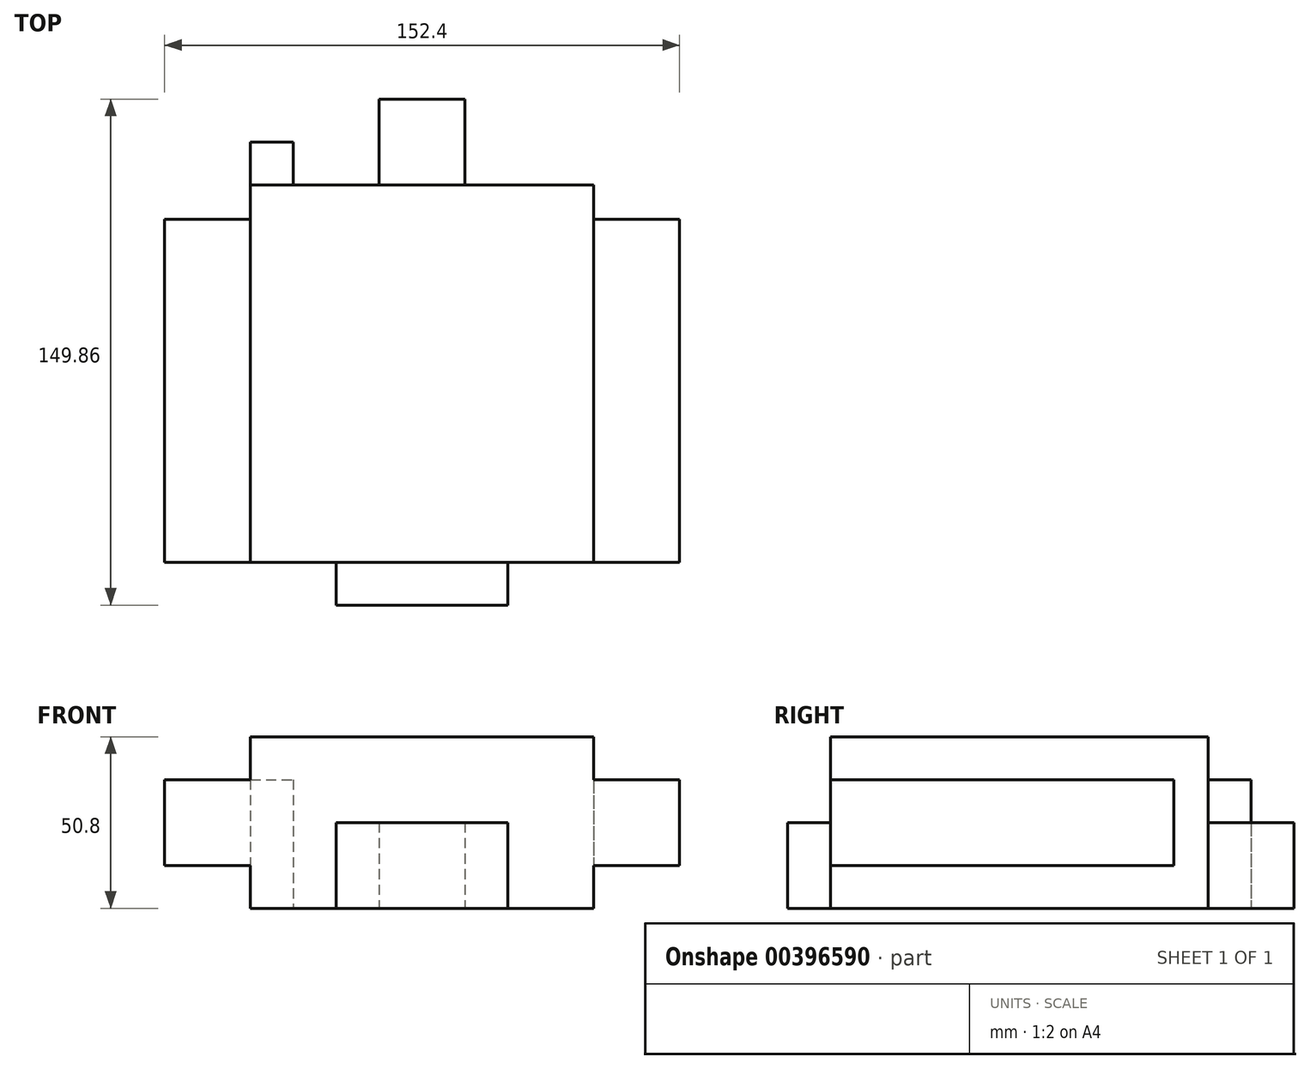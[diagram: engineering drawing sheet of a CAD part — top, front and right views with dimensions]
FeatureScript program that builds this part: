
annotation { "Feature Type Name" : "Feature", "Feature Type Description" : "" }
export const myFeature = defineFeature(function(context is Context, id is Id, definition is map)
    precondition{}
    {
        {
            var Q0;
            Q0=qCreatedBy(makeId("Top.planeOp"),FACE);
            var sketch = newSketch(context, id + "F0", { "sketchPlane" : qUnion([Q0])});
            skLineSegment(sketch, "E0.left", {"start": v(-50.8, -55.88) * mm, "end": v(-50.8, 55.88) * mm});
            skLineSegment(sketch, "E0.right", {"start": v(50.8, -55.88) * mm, "end": v(50.8, 55.88) * mm});
            skLineSegment(sketch, "E1", {"start": v(50.8, -55.88) * mm, "end": v(25.4, -55.88) * mm});
            skLineSegment(sketch, "E2", {"start": v(-25.4, -55.88) * mm, "end": v(-50.8, -55.88) * mm});
            skLineSegment(sketch, "E3.left", {"start": v(-25.4, -55.88) * mm, "end": v(-25.4, -55.88) * mm});
            skLineSegment(sketch, "E3.right", {"start": v(25.4, -55.88) * mm, "end": v(25.4, -55.88) * mm});
            skLineSegment(sketch, "E4.top", {"start": v(-25.4, -68.58) * mm, "end": v(25.4, -68.58) * mm});
            skLineSegment(sketch, "E4.left", {"start": v(-25.4, -55.88) * mm, "end": v(-25.4, -68.58) * mm});
            skLineSegment(sketch, "E4.right", {"start": v(25.4, -55.88) * mm, "end": v(25.4, -68.58) * mm});
            skLineSegment(sketch, "E5", {"start": v(25.4, -68.58) * mm, "end": v(12.7, -68.58) * mm});
            skLineSegment(sketch, "E6", {"start": v(-25.4, -68.58) * mm, "end": v(-12.7, -68.58) * mm});
            skLineSegment(sketch, "E7.left", {"start": v(-12.7, 55.88) * mm, "end": v(-12.7, 55.88) * mm});
            skLineSegment(sketch, "E7.right", {"start": v(12.7, 55.88) * mm, "end": v(12.7, 55.88) * mm});
            skLineSegment(sketch, "E8.top", {"start": v(-12.7, 81.28) * mm, "end": v(12.7, 81.28) * mm});
            skLineSegment(sketch, "E8.left", {"start": v(-12.7, 55.88) * mm, "end": v(-12.7, 81.28) * mm});
            skLineSegment(sketch, "E8.right", {"start": v(12.7, 55.88) * mm, "end": v(12.7, 81.28) * mm});
            skLineSegment(sketch, "E9", {"start": v(-12.7, 55.88) * mm, "end": v(-50.8, 55.88) * mm});
            skLineSegment(sketch, "E10", {"start": v(12.7, 55.88) * mm, "end": v(50.8, 55.88) * mm});
            skLineSegment(sketch, "E11", {"start": v(-12.7, 55.88) * mm, "end": v(12.7, 55.88) * mm});
            skLineSegment(sketch, "E12", {"start": v(25.4, -55.88) * mm, "end": v(-25.4, -55.88) * mm});
            skSolve(sketch);
        }
        {
            var Q0;
            Q0=makeQuery(id+"F0.imprint","IMPRINT",FACE,{"disambiguationData":[TD([[makeQuery(id+"F0.imprint","IMPRINT",EDGE,{"derivedFrom":sQuery(id+"F0.wireOp",EDGE,"E0.left")}),-1.0]])]});
            extrude(context, id + "F1", {"entities" : qUnion([Q0]), "depth" : 50.8 * mm});
        }
        {
            var Q0;
            Q0=makeQuery(id+"F0.imprint","IMPRINT",FACE,{"disambiguationData":[TD([[makeQuery(id+"F0.imprint","IMPRINT",EDGE,{"derivedFrom":sQuery(id+"F0.wireOp",EDGE,"E4.top")}),1.0]])]});
            extrude(context, id + "F2", {"entities" : qUnion([Q0]), "operationType" : NewBodyOperationType.ADD, "depth" : 25.4 * mm});
        }
        {
            var Q0;
            Q0=makeQuery(id+"F0.imprint","IMPRINT",FACE,{"disambiguationData":[TD([[makeQuery(id+"F0.imprint","IMPRINT",EDGE,{"derivedFrom":sQuery(id+"F0.wireOp",EDGE,"E8.top")}),-1.0]])]});
            extrude(context, id + "F3", {"entities" : qUnion([Q0]), "operationType" : NewBodyOperationType.ADD, "depth" : 25.4 * mm});
        }
        {
            var Q0;
            Q0=makeQuery(id+"F1.opExtrude","SWEPT_FACE",FACE,{"disambiguationData":[OSD([sQuery(id+"F0.wireOp",EDGE,"E1"),sQuery(id+"F0.wireOp",EDGE,"E2"),sQuery(id+"F0.wireOp",EDGE,"E12")])]});
            var sketch = newSketch(context, id + "F4", { "sketchPlane" : qUnion([Q0])});
            skLineSegment(sketch, "E13", {"start": v(-50.8, 50.8) * mm, "end": v(-50.8, 38.1) * mm});
            skLineSegment(sketch, "E14", {"start": v(-50.8, 38.1) * mm, "end": v(50.8, 38.1) * mm});
            skLineSegment(sketch, "E15", {"start": v(50.8, 38.1) * mm, "end": v(50.8, 50.8) * mm});
            skLineSegment(sketch, "E16", {"start": v(-50.8, 0) * mm, "end": v(-50.8, 12.7) * mm});
            skLineSegment(sketch, "E17", {"start": v(-50.8, 12.7) * mm, "end": v(50.8, 12.7) * mm});
            skLineSegment(sketch, "E18", {"start": v(50.8, 12.7) * mm, "end": v(50.8, 0) * mm});
            skLineSegment(sketch, "E19.bottom", {"start": v(-50.8, 38.1) * mm, "end": v(-50.8, 38.1) * mm});
            skLineSegment(sketch, "E19.top", {"start": v(-50.8, 12.7) * mm, "end": v(-50.8, 12.7) * mm});
            skLineSegment(sketch, "E19.left", {"start": v(-50.8, 38.1) * mm, "end": v(-50.8, 12.7) * mm});
            skLineSegment(sketch, "E19.right", {"start": v(-50.8, 38.1) * mm, "end": v(-50.8, 12.7) * mm});
            skLineSegment(sketch, "E20.bottom", {"start": v(-50.8, 38.1) * mm, "end": v(-76.2, 38.1) * mm});
            skLineSegment(sketch, "E20.top", {"start": v(-50.8, 12.7) * mm, "end": v(-76.2, 12.7) * mm});
            skLineSegment(sketch, "E20.right", {"start": v(-76.2, 38.1) * mm, "end": v(-76.2, 12.7) * mm});
            skLineSegment(sketch, "E21.bottom", {"start": v(50.8, 38.1) * mm, "end": v(76.2, 38.1) * mm});
            skLineSegment(sketch, "E21.top", {"start": v(50.8, 12.7) * mm, "end": v(76.2, 12.7) * mm});
            skLineSegment(sketch, "E21.left", {"start": v(50.8, 38.1) * mm, "end": v(50.8, 12.7) * mm});
            skLineSegment(sketch, "E21.right", {"start": v(76.2, 38.1) * mm, "end": v(76.2, 12.7) * mm});
            skSolve(sketch);
        }
        {
            var Q0;
            Q0=makeQuery(id+"F4.imprint","IMPRINT",FACE,{"disambiguationData":[TD([[makeQuery(id+"F4.imprint","IMPRINT",EDGE,{"derivedFrom":sQuery(id+"F4.wireOp",EDGE,"E20.bottom")}),1.0]])]});
            var Q1;
            Q1=makeQuery(id+"F4.imprint","IMPRINT",FACE,{"disambiguationData":[TD([[makeQuery(id+"F4.imprint","IMPRINT",EDGE,{"derivedFrom":sQuery(id+"F4.wireOp",EDGE,"E21.bottom")}),-1.0]])]});
            extrude(context, id + "F5", {"entities" : qUnion([Q0, Q1]), "operationType" : NewBodyOperationType.ADD, "oppositeDirection" : true, "depth" : 101.6 * mm});
        }
        {
            var Q0;
            {var subQ0=sQuery(id+"F0.wireOp",EDGE,"E11");var subQ1=sQuery(id+"F0.wireOp",EDGE,"E12");Q0=makeQuery(id+"F3.boolean.opBoolean","MERGE",FACE,{"derivedFrom":[makeQuery(id+"F2.boolean.opBoolean","MERGE",FACE,{"derivedFrom":[makeQuery(id+"F1.opExtrude","CAP_FACE",FACE,{"disambiguationData":[OSD([sQuery(id+"F0.wireOp",EDGE,"E0.left"),sQuery(id+"F0.wireOp",EDGE,"E0.right"),sQuery(id+"F0.wireOp",EDGE,"E1"),sQuery(id+"F0.wireOp",EDGE,"E2"),sQuery(id+"F0.wireOp",EDGE,"E9"),sQuery(id+"F0.wireOp",EDGE,"E10"),subQ0,subQ1])],"isStart":true}),makeQuery(id+"F2.opExtrude","CAP_FACE",FACE,{"disambiguationData":[OSD([sQuery(id+"F0.wireOp",EDGE,"E4.top"),sQuery(id+"F0.wireOp",EDGE,"E4.left"),sQuery(id+"F0.wireOp",EDGE,"E4.right"),sQuery(id+"F0.wireOp",EDGE,"E5"),sQuery(id+"F0.wireOp",EDGE,"E6"),subQ1])],"isStart":true})]}),makeQuery(id+"F3.opExtrude","CAP_FACE",FACE,{"disambiguationData":[OSD([sQuery(id+"F0.wireOp",EDGE,"E8.top"),sQuery(id+"F0.wireOp",EDGE,"E8.left"),sQuery(id+"F0.wireOp",EDGE,"E8.right"),subQ0])],"isStart":true})]});}
            var sketch = newSketch(context, id + "F6", { "sketchPlane" : qUnion([Q0])});
            skLineSegment(sketch, "E22", {"start": v(-50.8, -55.88) * mm, "end": v(-38.1, -55.88) * mm});
            skLineSegment(sketch, "E23", {"start": v(50.8, -55.88) * mm, "end": v(38.1, -55.88) * mm});
            skLineSegment(sketch, "E24.top", {"start": v(-50.8, -68.58) * mm, "end": v(-38.1, -68.58) * mm});
            skLineSegment(sketch, "E24.left", {"start": v(-50.8, -55.88) * mm, "end": v(-50.8, -68.58) * mm});
            skLineSegment(sketch, "E24.right", {"start": v(-38.1, -55.88) * mm, "end": v(-38.1, -68.58) * mm});
            skLineSegment(sketch, "E25.bottom", {"start": v(38.1, -55.88) * mm, "end": v(50.8, -55.88) * mm});
            skLineSegment(sketch, "E25.top", {"start": v(38.1, -55.88) * mm, "end": v(50.8, -55.88) * mm});
            skLineSegment(sketch, "E25.left", {"start": v(38.1, -55.88) * mm, "end": v(38.1, -55.88) * mm});
            skLineSegment(sketch, "E25.right", {"start": v(50.8, -55.88) * mm, "end": v(50.8, -55.88) * mm});
            skLineSegment(sketch, "E26.top", {"start": v(38.1, -68.58) * mm, "end": v(50.8, -68.58) * mm});
            skLineSegment(sketch, "E26.left", {"start": v(38.1, -55.88) * mm, "end": v(38.1, -68.58) * mm});
            skLineSegment(sketch, "E26.right", {"start": v(50.8, -55.88) * mm, "end": v(50.8, -68.58) * mm});
            skSolve(sketch);
        }
        {
            var Q0;
            Q0=makeQuery(id+"F6.imprint","IMPRINT",FACE,{"disambiguationData":[TD([[makeQuery(id+"F6.imprint","IMPRINT",EDGE,{"derivedFrom":sQuery(id+"F6.wireOp",EDGE,"E22")}),-1.0]])]});
            var Q1;
            Q1=makeQuery(id+"F6.imprint","IMPRINT",FACE,{"disambiguationData":[TD([[makeQuery(id+"F6.imprint","IMPRINT",EDGE,{"derivedFrom":sQuery(id+"F6.wireOp",EDGE,"E25.bottom")}),-1.0]])]});
            extrude(context, id + "F7", {"entities" : qUnion([Q0, Q1]), "operationType" : NewBodyOperationType.ADD, "oppositeDirection" : true, "depth" : 38.1 * mm});
        }
    });
